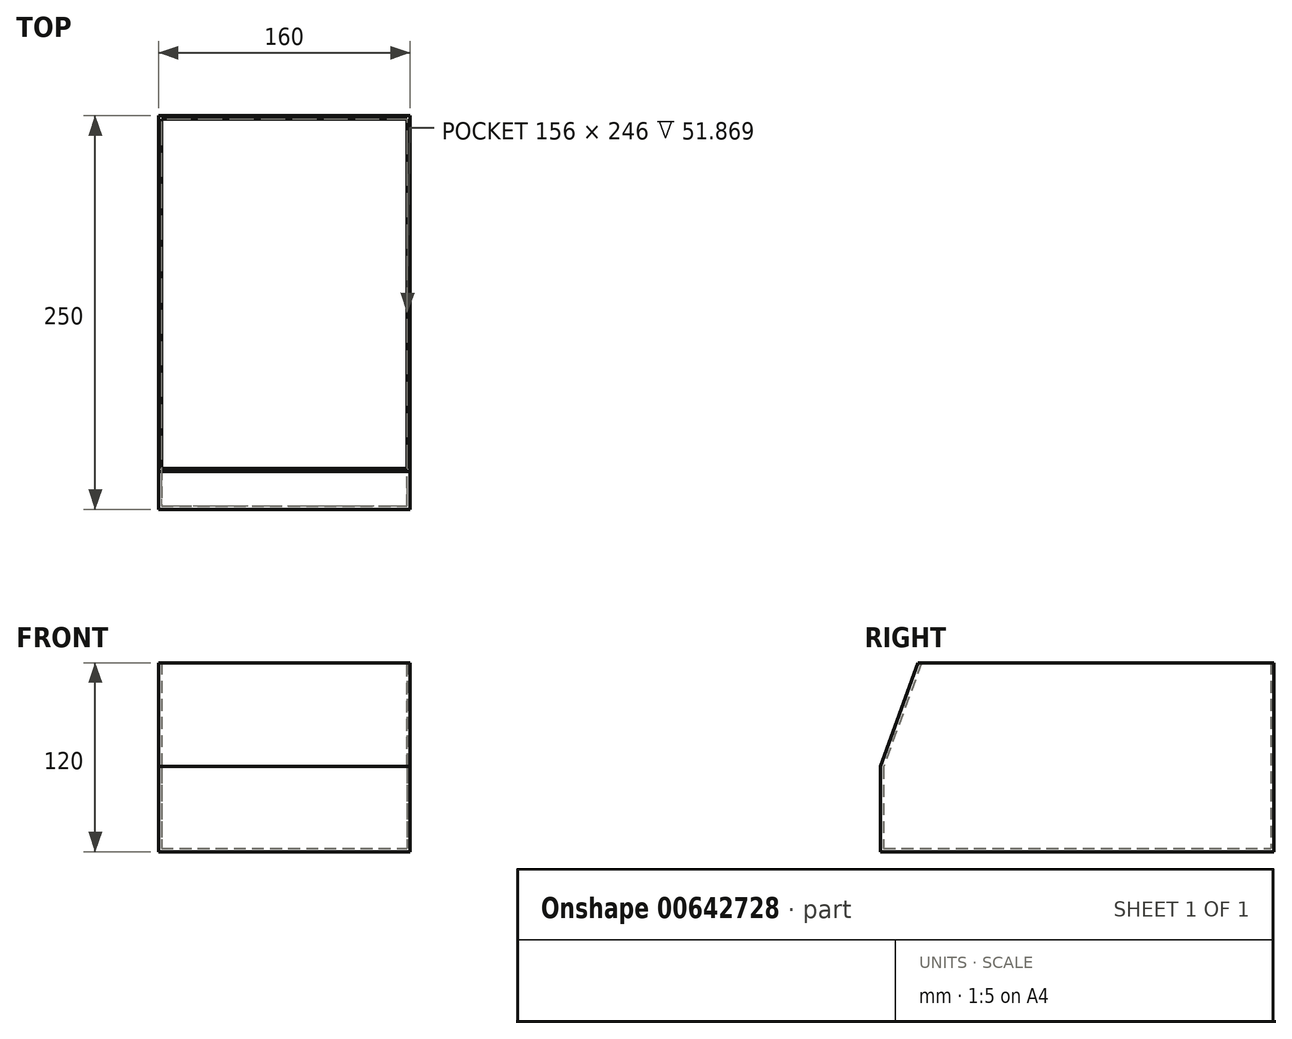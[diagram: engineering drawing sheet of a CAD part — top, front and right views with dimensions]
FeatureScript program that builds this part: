
annotation { "Feature Type Name" : "Feature", "Feature Type Description" : "" }
export const myFeature = defineFeature(function(context is Context, id is Id, definition is map)
    precondition{}
    {
        {
            var Q0;
            Q0=qCreatedBy(makeId("Front.planeOp"),FACE);
            var sketch = newSketch(context, id + "F0", { "sketchPlane" : qUnion([Q0])});
            skLineSegment(sketch, "E0.bottom", {"start": v(-47.2, 73.43) * mm, "end": v(72.8, 73.43) * mm});
            skLineSegment(sketch, "E0.top", {"start": v(-47.2, -46.57) * mm, "end": v(72.8, -46.57) * mm});
            skLineSegment(sketch, "E0.left", {"start": v(-47.2, 73.43) * mm, "end": v(-47.2, -46.57) * mm});
            skLineSegment(sketch, "E0.right", {"start": v(72.8, 73.43) * mm, "end": v(72.8, -46.57) * mm, "construction": true});
            skLineSegment(sketch, "E1", {"start": v(72.8, 73.43) * mm, "end": v(112.8, 73.43) * mm});
            skLineSegment(sketch, "E2", {"start": v(112.8, 73.43) * mm, "end": v(112.8, -46.57) * mm});
            skLineSegment(sketch, "E3", {"start": v(112.8, -46.57) * mm, "end": v(72.8, -46.57) * mm});
            skSolve(sketch);
        }
        {
            var Q0;
            Q0=makeQuery(id+"F0.imprint","IMPRINT",FACE,{"disambiguationData":[TD([[makeQuery(id+"F0.imprint","IMPRINT",EDGE,{"derivedFrom":sQuery(id+"F0.wireOp",EDGE,"E0.bottom")}),-1.0]])]});
            extrude(context, id + "F1", {"entities" : qUnion([Q0]), "depth" : 250 * mm, "offsetDistance" : 25 * mm});
        }
        {
            var Q0;
            Q0=makeQuery(id+"F1.opExtrude","SWEPT_FACE",FACE,{"disambiguationData":[OSD([sQuery(id+"F0.wireOp",EDGE,"E2")])]});
            var sketch = newSketch(context, id + "F2", { "sketchPlane" : qUnion([Q0])});
            skLineSegment(sketch, "E4", {"start": v(-250, 7.66) * mm, "end": v(-226.06, 73.43) * mm});
            skLineSegment(sketch, "E5.bottom", {"start": v(0, -46.57) * mm, "end": v(-142, -46.57) * mm});
            skLineSegment(sketch, "E5.top", {"start": v(0, 39.43) * mm, "end": v(-142, 39.43) * mm, "construction": true});
            skLineSegment(sketch, "E5.left", {"start": v(0, -46.57) * mm, "end": v(0, 39.43) * mm});
            skLineSegment(sketch, "E5.right", {"start": v(-142, -46.57) * mm, "end": v(-142, 39.43) * mm, "construction": true});
            skLineSegment(sketch, "E6", {"start": v(-2, 39.43) * mm, "end": v(-2, -46.57) * mm, "construction": true});
            skSolve(sketch);
        }
        {
            var Q0;
            {var subQ0=sQuery(id+"F2.wireOp",EDGE,"E4");Q0=makeQuery(id+"F2.imprint","IMPRINT",FACE,{"disambiguationData":[TD([[makeQuery(id+"F2.imprint","IMPRINT",EDGE,{"derivedFrom":subQ0}),1.0]])]});}
            extrude(context, id + "F3", {"entities" : qUnion([Q0]), "operationType" : NewBodyOperationType.REMOVE, "endBound" : BoundingType.UP_TO_NEXT, "oppositeDirection" : true, "depth" : 25 * mm, "offsetDistance" : 25 * mm});
        }
        {
            var Q0;
            Q0=makeQuery(id+"F1.opExtrude","SWEPT_FACE",FACE,{"disambiguationData":[OSD([sQuery(id+"F0.wireOp",EDGE,"E0.bottom"),sQuery(id+"F0.wireOp",EDGE,"E1")])]});
            shell(context, id + "F4", {"entities" : qUnion([Q0]), "thickness" : 2 * mm});
        }
    });
